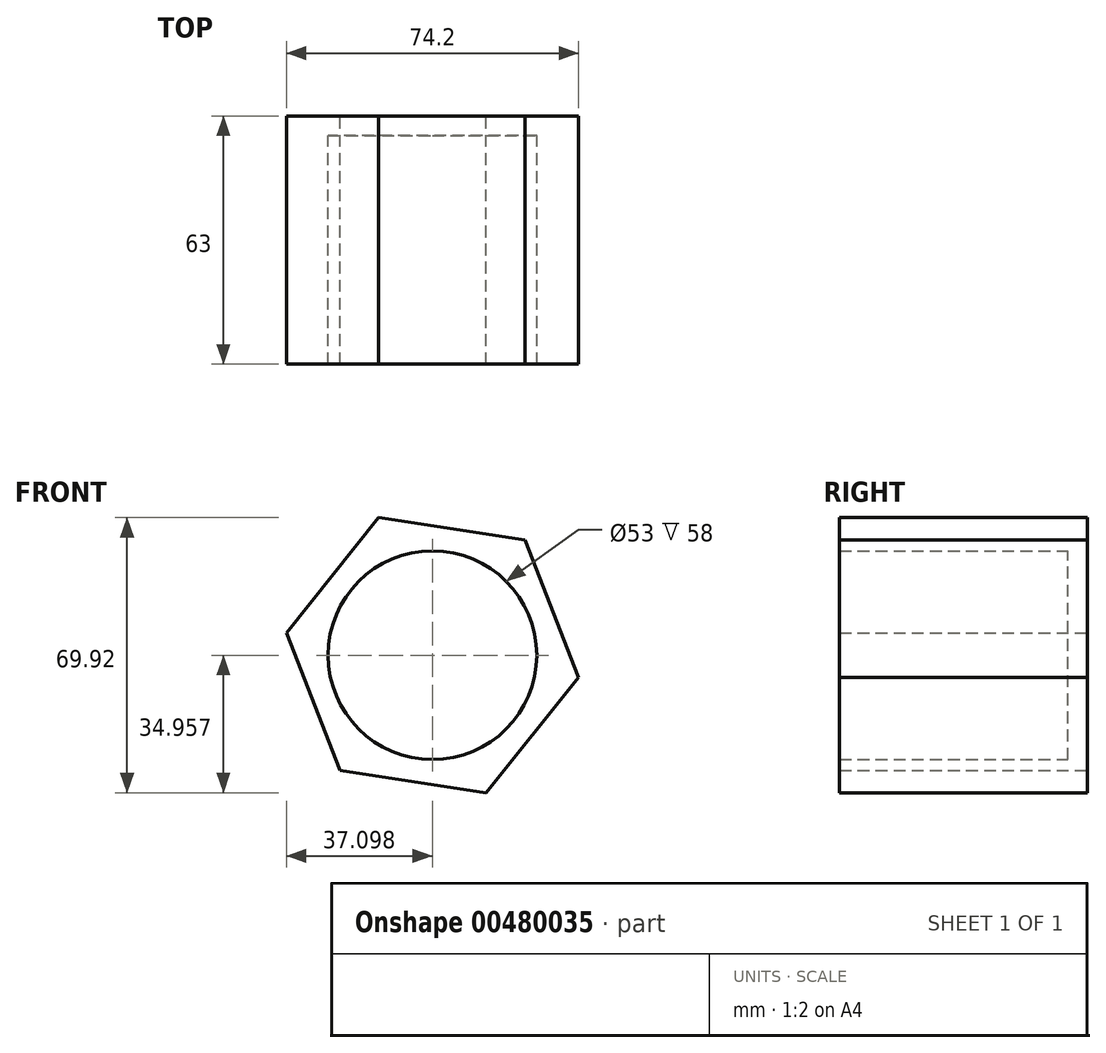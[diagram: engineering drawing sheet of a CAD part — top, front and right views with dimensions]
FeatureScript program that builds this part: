
annotation { "Feature Type Name" : "Feature", "Feature Type Description" : "" }
export const myFeature = defineFeature(function(context is Context, id is Id, definition is map)
    precondition{}
    {
        {
            var Q0;
            Q0=qCreatedBy(makeId("Front.planeOp"),FACE);
            var sketch = newSketch(context, id + "F0", { "sketchPlane" : qUnion([Q0])});
            skCircle(sketch, "E0.cCircle", {"center": v(-9.9, -5) * mm, "radius": 32.5 * mm, "construction": true});
            skLineSegment(sketch, "E0.0", {"start": v(27.2, -10.66) * mm, "end": v(3.74, -39.95) * mm});
            skLineSegment(sketch, "E0.1", {"start": v(3.74, -39.95) * mm, "end": v(-33.35, -34.3) * mm});
            skLineSegment(sketch, "E0.2", {"start": v(-33.35, -34.3) * mm, "end": v(-47, 0.67) * mm});
            skLineSegment(sketch, "E0.3", {"start": v(-47, 0.67) * mm, "end": v(-23.55, 29.97) * mm});
            skLineSegment(sketch, "E0.4", {"start": v(-23.55, 29.97) * mm, "end": v(13.55, 24.3) * mm});
            skLineSegment(sketch, "E0.5", {"start": v(13.55, 24.3) * mm, "end": v(27.2, -10.66) * mm});
            skPoint(sketch, "E0.0.midPoint", {"position": v(15.47, -25.3) * mm});
            skCircle(sketch, "E1", {"center": v(-9.9, -5) * mm, "radius": 26.5 * mm});
            skSolve(sketch);
        }
        {
            var Q0;
            Q0=qSketchRegion(id+"F0",true);
            extrude(context, id + "F1", {"entities" : qUnion([Q0]), "depth" : 58 * mm});
        }
        {
            var Q0;
            Q0=makeQuery(id+"F1.opExtrude","CAP_FACE",FACE,{"disambiguationData":[OSD([sQuery(id+"F0.wireOp",EDGE,"E0.0"),sQuery(id+"F0.wireOp",EDGE,"E0.1"),sQuery(id+"F0.wireOp",EDGE,"E0.2"),sQuery(id+"F0.wireOp",EDGE,"E0.3"),sQuery(id+"F0.wireOp",EDGE,"E0.4"),sQuery(id+"F0.wireOp",EDGE,"E0.5"),sQuery(id+"F0.wireOp",EDGE,"E1")])],"isStart":true});
            var sketch = newSketch(context, id + "F2", { "sketchPlane" : qUnion([Q0])});
            skLineSegment(sketch, "E2.0.0", {"start": v(-13.55, 24.3) * mm, "end": v(-27.2, -10.66) * mm});
            skLineSegment(sketch, "E2.0.1", {"start": v(-27.2, -10.66) * mm, "end": v(-3.74, -39.95) * mm});
            skLineSegment(sketch, "E2.0.2", {"start": v(-3.74, -39.95) * mm, "end": v(33.35, -34.3) * mm});
            skLineSegment(sketch, "E2.0.3", {"start": v(33.35, -34.3) * mm, "end": v(47, 0.67) * mm});
            skLineSegment(sketch, "E2.0.4", {"start": v(47, 0.67) * mm, "end": v(23.55, 29.97) * mm});
            skLineSegment(sketch, "E2.0.5", {"start": v(23.55, 29.97) * mm, "end": v(-13.55, 24.3) * mm});
            skSolve(sketch);
        }
        {
            var Q0;
            Q0=qSketchRegion(id+"F2",true);
            extrude(context, id + "F3", {"entities" : qUnion([Q0]), "operationType" : NewBodyOperationType.ADD, "depth" : 5 * mm});
        }
    });
